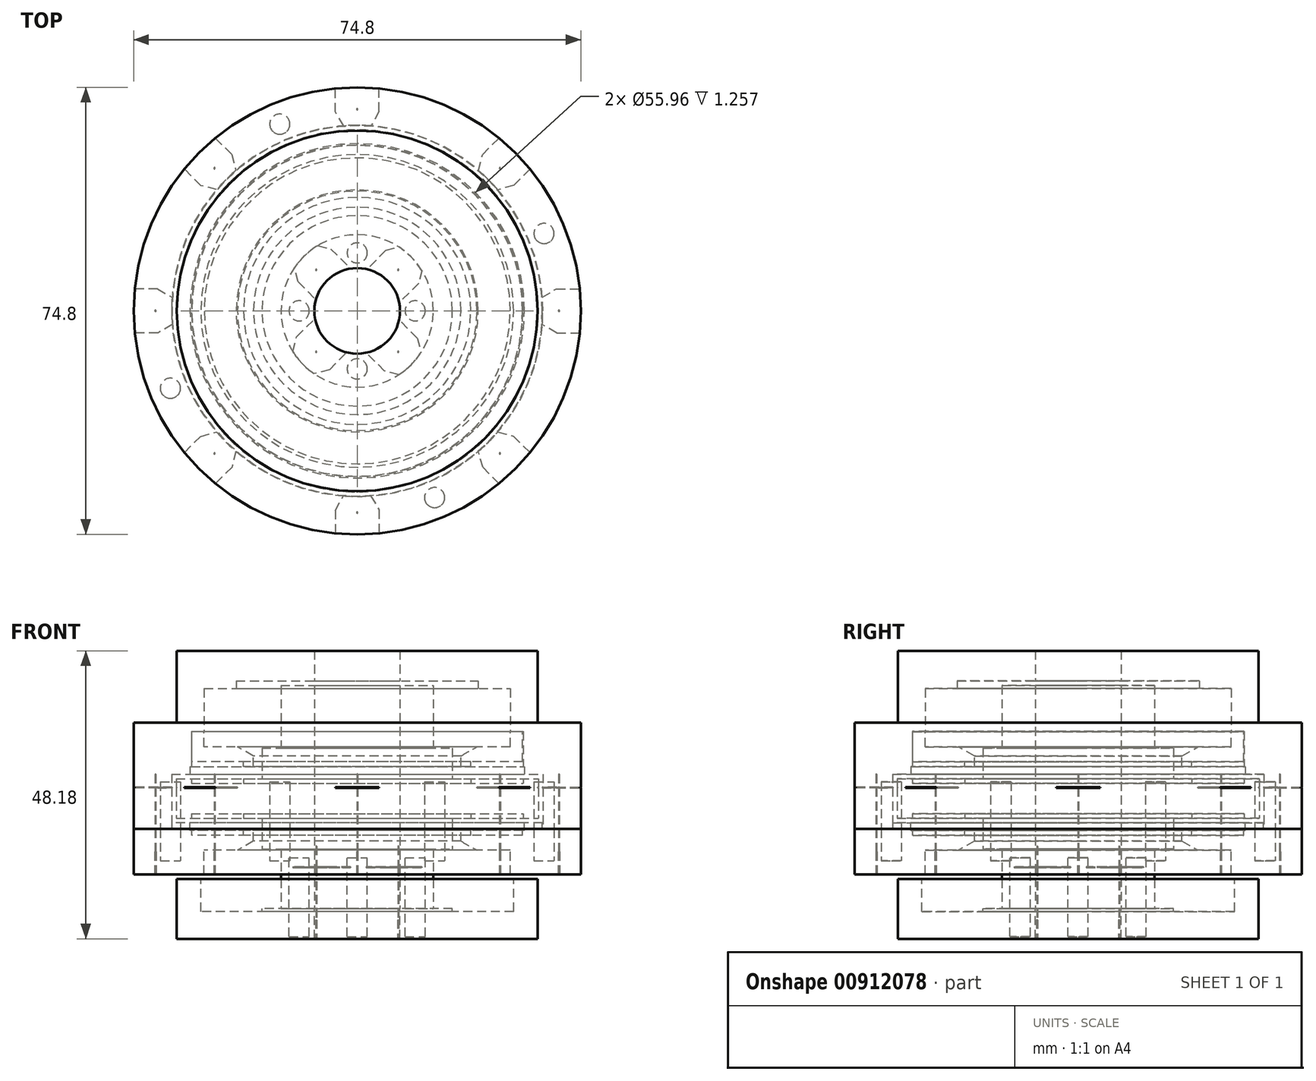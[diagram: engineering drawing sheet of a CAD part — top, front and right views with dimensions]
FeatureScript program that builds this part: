
annotation { "Feature Type Name" : "Feature", "Feature Type Description" : "" }
export const myFeature = defineFeature(function(context is Context, id is Id, definition is map)
    precondition{}
    {
        {
            assignVariable(context, id + "F0", {"name" : "CLOSE_FIT", "anyValue" : 0.01});
        }
        {
            assignVariable(context, id + "F1", {"name" : "SHRINKAGE", "anyValue" : 0});
        }
        {
            var Q0;
            Q0=qCreatedBy(makeId("Front.planeOp"),FACE);
            var sketch = newSketch(context, id + "F2", { "sketchPlane" : qUnion([Q0])});
            skLineSegment(sketch, "E0", {"start": v(-19.08, 2.54) * mm, "end": v(-19.08, 6.13) * mm});
            skLineSegment(sketch, "E1", {"start": v(-19.08, 6.13) * mm, "end": v(-27.67, 6.13) * mm});
            skLineSegment(sketch, "E2", {"start": v(-27.67, 6.13) * mm, "end": v(-27.67, 2.54) * mm});
            skLineSegment(sketch, "E3", {"start": v(-19.08, 2.54) * mm, "end": v(-27.67, 2.54) * mm});
            skLineSegment(sketch, "E4.bottom", {"start": v(-27.67, -2.54) * mm, "end": v(-19.08, -2.54) * mm});
            skLineSegment(sketch, "E4.top", {"start": v(-27.67, -6.13) * mm, "end": v(-19.08, -6.13) * mm});
            skLineSegment(sketch, "E4.left", {"start": v(-27.67, -2.54) * mm, "end": v(-27.67, -6.13) * mm});
            skLineSegment(sketch, "E4.right", {"start": v(-19.08, -2.54) * mm, "end": v(-19.08, -6.13) * mm});
            skLineSegment(sketch, "E5", {"start": v(-27.67, 5.33) * mm, "end": v(-27.93, 5.33) * mm});
            skLineSegment(sketch, "E6", {"start": v(-27.93, 5.33) * mm, "end": v(-27.93, 3.34) * mm});
            skLineSegment(sketch, "E7", {"start": v(-27.93, 3.34) * mm, "end": v(-27.67, 3.34) * mm});
            skLineSegment(sketch, "E8", {"start": v(-19.08, 5.33) * mm, "end": v(-18.83, 5.33) * mm});
            skLineSegment(sketch, "E9", {"start": v(-18.83, 5.33) * mm, "end": v(-18.83, 3.34) * mm});
            skLineSegment(sketch, "E10", {"start": v(-18.83, 3.34) * mm, "end": v(-19.08, 3.34) * mm});
            skLineSegment(sketch, "E11", {"start": v(-27.67, -3.35) * mm, "end": v(-27.93, -3.35) * mm});
            skLineSegment(sketch, "E12", {"start": v(-27.93, -3.35) * mm, "end": v(-27.93, -5.32) * mm});
            skLineSegment(sketch, "E13", {"start": v(-27.93, -5.32) * mm, "end": v(-27.67, -5.32) * mm});
            skLineSegment(sketch, "E14", {"start": v(-19.08, -3.35) * mm, "end": v(-18.83, -3.35) * mm});
            skLineSegment(sketch, "E15", {"start": v(-18.83, -3.35) * mm, "end": v(-18.83, -5.32) * mm});
            skLineSegment(sketch, "E16", {"start": v(-18.83, -5.32) * mm, "end": v(-19.08, -5.32) * mm});
            skSolve(sketch);
        }
        {
            var Q0;
            Q0=qCreatedBy(makeId("Front.planeOp"),FACE);
            var sketch = newSketch(context, id + "F3", { "sketchPlane" : qUnion([Q0])});
            skLineSegment(sketch, "E17", {"start": v(-25.4, 18.14) * mm, "end": v(-25.4, 8.67) * mm});
            skLineSegment(sketch, "E18", {"start": v(-25.4, 8.67) * mm, "end": v(-12.7, 8.67) * mm});
            skLineSegment(sketch, "E19", {"start": v(-12.7, 8.67) * mm, "end": v(-12.7, 18.14) * mm});
            skLineSegment(sketch, "E20", {"start": v(-12.7, 18.14) * mm, "end": v(-25.4, 18.14) * mm});
            skLineSegment(sketch, "E21", {"start": v(0, 0) * mm, "end": v(0, 56.46) * mm, "construction": true});
            skLineSegment(sketch, "E22.bottom", {"start": v(-25.4, -8.67) * mm, "end": v(-12.7, -8.67) * mm});
            skLineSegment(sketch, "E22.top", {"start": v(-25.4, -18.14) * mm, "end": v(-12.7, -18.14) * mm});
            skLineSegment(sketch, "E22.left", {"start": v(-25.4, -8.67) * mm, "end": v(-25.4, -18.14) * mm});
            skLineSegment(sketch, "E22.right", {"start": v(-12.7, -8.67) * mm, "end": v(-12.7, -18.14) * mm});
            skSolve(sketch);
        }
        {
            var Q0;
            Q0=qCreatedBy(makeId("Front.planeOp"),FACE);
            var sketch = newSketch(context, id + "F4", { "sketchPlane" : qUnion([Q0])});
            skLineSegment(sketch, "E23", {"start": v(-30.18, 31.75) * mm, "end": v(-26, 31.75) * mm});
            skLineSegment(sketch, "E24", {"start": v(-26, 31.75) * mm, "end": v(-26, 82.55) * mm});
            skLineSegment(sketch, "E25", {"start": v(-26, 82.55) * mm, "end": v(-30.18, 82.55) * mm});
            skLineSegment(sketch, "E26", {"start": v(-30.18, 82.55) * mm, "end": v(-30.18, 31.75) * mm});
            skLineSegment(sketch, "E27.bottom", {"start": v(-30.18, -31.75) * mm, "end": v(-26, -31.75) * mm});
            skLineSegment(sketch, "E27.top", {"start": v(-30.18, -82.55) * mm, "end": v(-26, -82.55) * mm});
            skLineSegment(sketch, "E27.left", {"start": v(-30.18, -31.75) * mm, "end": v(-30.18, -82.55) * mm});
            skLineSegment(sketch, "E27.right", {"start": v(-26, -31.75) * mm, "end": v(-26, -82.55) * mm});
            skSolve(sketch);
        }
        {
            var Q0;
            Q0=qCreatedBy(makeId("Front.planeOp"),FACE);
            var sketch = newSketch(context, id + "F5", { "sketchPlane" : qUnion([Q0])});
            skLineSegment(sketch, "E28", {"start": v(-27.75, -2.54) * mm, "end": v(-19, -2.54) * mm});
            skLineSegment(sketch, "E29", {"start": v(-12.75, -8.42) * mm, "end": v(-12.75, -18.39) * mm});
            skLineSegment(sketch, "E30", {"start": v(-27.75, 2.54) * mm, "end": v(-19, 2.54) * mm});
            skLineSegment(sketch, "E31", {"start": v(-12.75, 8.42) * mm, "end": v(-12.75, 18.9) * mm});
            skLineSegment(sketch, "E32", {"start": v(-12.75, 18.9) * mm, "end": v(-7.16, 18.9) * mm});
            skLineSegment(sketch, "E33", {"start": v(-7.16, 18.9) * mm, "end": v(-7.16, -18.39) * mm});
            skLineSegment(sketch, "E34", {"start": v(-7.16, -18.39) * mm, "end": v(-12.75, -18.39) * mm});
            skLineSegment(sketch, "E35", {"start": v(-19, 2.54) * mm, "end": v(-19, 3.33) * mm});
            skLineSegment(sketch, "E36", {"start": v(-19, 3.33) * mm, "end": v(-15.93, 3.33) * mm});
            skLineSegment(sketch, "E37", {"start": v(-15.93, 3.33) * mm, "end": v(-15.93, 8.42) * mm});
            skLineSegment(sketch, "E38", {"start": v(-15.93, 8.42) * mm, "end": v(-12.75, 8.42) * mm});
            skLineSegment(sketch, "E39", {"start": v(-19, -2.54) * mm, "end": v(-19, -3.33) * mm});
            skLineSegment(sketch, "E40", {"start": v(-19, -3.33) * mm, "end": v(-15.93, -3.33) * mm});
            skLineSegment(sketch, "E41", {"start": v(-15.93, -3.33) * mm, "end": v(-15.93, -8.42) * mm});
            skLineSegment(sketch, "E42", {"start": v(-15.93, -8.42) * mm, "end": v(-12.75, -8.42) * mm});
            skLineSegment(sketch, "E43", {"start": v(-27.75, 2.54) * mm, "end": v(-27.75, 3.33) * mm});
            skLineSegment(sketch, "E44", {"start": v(-27.75, 3.33) * mm, "end": v(-30.29, 3.33) * mm});
            skLineSegment(sketch, "E45", {"start": v(-30.29, -3.33) * mm, "end": v(-27.75, -3.33) * mm});
            skLineSegment(sketch, "E46", {"start": v(-27.75, -3.33) * mm, "end": v(-27.75, -2.54) * mm});
            skLineSegment(sketch, "E47", {"start": v(-30.29, 3.33) * mm, "end": v(-30.29, -3.33) * mm});
            skSolve(sketch);
        }
        {
            var Q0;
            Q0=qCreatedBy(makeId("Front.planeOp"),FACE);
            var sketch = newSketch(context, id + "F6", { "sketchPlane" : qUnion([Q0])});
            skLineSegment(sketch, "E48", {"start": v(-20.24, 18.39) * mm, "end": v(-25.6, 18.39) * mm});
            skLineSegment(sketch, "E49", {"start": v(-25.6, 18.39) * mm, "end": v(-25.6, 11.21) * mm});
            skLineSegment(sketch, "E50", {"start": v(-37.4, -5.08) * mm, "end": v(-31.05, -5.08) * mm});
            skLineSegment(sketch, "E51", {"start": v(-31.05, -5.08) * mm, "end": v(-31.05, 4.09) * mm});
            skLineSegment(sketch, "E52", {"start": v(-31.05, 4.09) * mm, "end": v(-27.98, 4.09) * mm});
            skLineSegment(sketch, "E53", {"start": v(-27.75, 5.35) * mm, "end": v(-27.75, 11.21) * mm});
            skLineSegment(sketch, "E54", {"start": v(-27.75, 11.21) * mm, "end": v(-25.6, 11.21) * mm});
            skLineSegment(sketch, "E55", {"start": v(-20.24, 18.39) * mm, "end": v(-20.24, 19.66) * mm});
            skLineSegment(sketch, "E56", {"start": v(-37.4, -5.08) * mm, "end": v(-37.4, 12.7) * mm});
            skLineSegment(sketch, "E57", {"start": v(-30.18, 24.71) * mm, "end": v(-30.18, 12.7) * mm});
            skLineSegment(sketch, "E58", {"start": v(-30.18, 12.7) * mm, "end": v(-37.4, 12.7) * mm});
            skLineSegment(sketch, "E59", {"start": v(0, 0) * mm, "end": v(0, 39.51) * mm, "construction": true});
            skLineSegment(sketch, "E60", {"start": v(-7.16, 24.71) * mm, "end": v(-7.16, 19.66) * mm});
            skLineSegment(sketch, "E61", {"start": v(-7.16, 19.66) * mm, "end": v(-20.24, 19.66) * mm});
            skLineSegment(sketch, "E62", {"start": v(-27.98, 4.09) * mm, "end": v(-27.98, 5.35) * mm});
            skLineSegment(sketch, "E63", {"start": v(-27.98, 5.35) * mm, "end": v(-27.75, 5.35) * mm});
            skLineSegment(sketch, "E64", {"start": v(-30.18, 24.71) * mm, "end": v(-7.16, 24.71) * mm});
            skSolve(sketch);
        }
        {
            var Q0;
            Q0=qCreatedBy(makeId("Front.planeOp"),FACE);
            var sketch = newSketch(context, id + "F7", { "sketchPlane" : qUnion([Q0])});
            skLineSegment(sketch, "E65", {"start": v(-27.67, 6.13) * mm, "end": v(-19, 6.13) * mm});
            skLineSegment(sketch, "E66", {"start": v(-17.35, 7.13) * mm, "end": v(-20.04, 8.65) * mm});
            skLineSegment(sketch, "E67", {"start": v(-20.04, 8.65) * mm, "end": v(-25.6, 8.65) * mm});
            skLineSegment(sketch, "E68", {"start": v(-25.6, 8.65) * mm, "end": v(-25.6, 11.19) * mm});
            skLineSegment(sketch, "E69", {"start": v(-25.6, 11.19) * mm, "end": v(-27.67, 11.19) * mm});
            skLineSegment(sketch, "E70", {"start": v(-27.67, 11.19) * mm, "end": v(-27.67, 6.13) * mm});
            skLineSegment(sketch, "E71", {"start": v(-19, 6.13) * mm, "end": v(-19, 5.35) * mm});
            skLineSegment(sketch, "E72", {"start": v(-19, 5.35) * mm, "end": v(-17.35, 5.35) * mm});
            skLineSegment(sketch, "E73", {"start": v(-17.35, 5.35) * mm, "end": v(-17.35, 7.13) * mm});
            skLineSegment(sketch, "E74", {"start": v(-30.05, 0) * mm, "end": v(0, 0) * mm, "construction": true});
            skLineSegment(sketch, "E75.MirrorCS", {"start": v(-19, -5.35) * mm, "end": v(-17.35, -5.35) * mm, "construction": true});
            skLineSegment(sketch, "E76.MirrorCS", {"start": v(-19, -6.13) * mm, "end": v(-19, -5.35) * mm, "construction": true});
            skLineSegment(sketch, "E77.MirrorCS", {"start": v(-25.6, -8.65) * mm, "end": v(-25.6, -11.19) * mm, "construction": true});
            skLineSegment(sketch, "E78.MirrorCS", {"start": v(-25.6, -11.19) * mm, "end": v(-27.67, -11.19) * mm, "construction": true});
            skLineSegment(sketch, "E79.MirrorCS", {"start": v(-17.35, -5.35) * mm, "end": v(-17.35, -7.13) * mm, "construction": true});
            skLineSegment(sketch, "E80.MirrorCS", {"start": v(-27.67, -6.13) * mm, "end": v(-19, -6.13) * mm, "construction": true});
            skLineSegment(sketch, "E81.MirrorCS", {"start": v(-20.04, -8.65) * mm, "end": v(-25.6, -8.65) * mm, "construction": true});
            skLineSegment(sketch, "E82.MirrorCS", {"start": v(-27.67, -11.19) * mm, "end": v(-27.67, -6.13) * mm, "construction": true});
            skLineSegment(sketch, "E83.MirrorCS", {"start": v(-17.35, -7.13) * mm, "end": v(-20.04, -8.65) * mm, "construction": true});
            skLineSegment(sketch, "E84", {"start": v(0, 19.57) * mm, "end": v(0, -21.08) * mm, "construction": true});
            skSolve(sketch);
        }
        {
            var Q0;
            Q0=qCreatedBy(makeId("Front.planeOp"),FACE);
            var sketch = newSketch(context, id + "F8", { "sketchPlane" : qUnion([Q0])});
            skLineSegment(sketch, "E85", {"start": v(-27.67, -11.19) * mm, "end": v(-25.6, -11.19) * mm});
            skLineSegment(sketch, "E86", {"start": v(-25.6, -11.19) * mm, "end": v(-25.6, -12.7) * mm});
            skLineSegment(sketch, "E87", {"start": v(-37.4, -5.1) * mm, "end": v(-37.4, -12.7) * mm});
            skLineSegment(sketch, "E88", {"start": v(-37.4, -12.7) * mm, "end": v(-25.6, -12.7) * mm});
            skLineSegment(sketch, "E89", {"start": v(-37.4, -5.1) * mm, "end": v(-30.98, -5.1) * mm});
            skLineSegment(sketch, "E90", {"start": v(-30.98, -4.09) * mm, "end": v(-27.98, -4.09) * mm});
            skLineSegment(sketch, "E91", {"start": v(-27.67, -5.35) * mm, "end": v(-27.67, -11.19) * mm});
            skLineSegment(sketch, "E92", {"start": v(0, 0) * mm, "end": v(0, -37.72) * mm, "construction": true});
            skLineSegment(sketch, "E93", {"start": v(-27.98, -4.09) * mm, "end": v(-27.98, -5.35) * mm});
            skLineSegment(sketch, "E94", {"start": v(-27.98, -5.35) * mm, "end": v(-27.67, -5.35) * mm});
            skLineSegment(sketch, "E95", {"start": v(-30.98, -4.09) * mm, "end": v(-30.98, -5.1) * mm});
            skLineSegment(sketch, "E96", {"start": v(-25.6, -11.19) * mm, "end": v(-25.6, -8.65) * mm});
            skLineSegment(sketch, "E97", {"start": v(-25.6, -8.65) * mm, "end": v(-20.04, -8.65) * mm});
            skLineSegment(sketch, "E98", {"start": v(-20.04, -8.65) * mm, "end": v(-17.35, -7.13) * mm});
            skLineSegment(sketch, "E99", {"start": v(-17.35, -7.13) * mm, "end": v(-17.35, -5.35) * mm});
            skLineSegment(sketch, "E100", {"start": v(-17.35, -5.35) * mm, "end": v(-19, -5.35) * mm});
            skLineSegment(sketch, "E101", {"start": v(-19, -5.35) * mm, "end": v(-19, -6.13) * mm});
            skLineSegment(sketch, "E102", {"start": v(-19, -6.13) * mm, "end": v(-27.67, -6.13) * mm});
            skSolve(sketch);
        }
        {
            var Q0;
            Q0=qCreatedBy(makeId("Front.planeOp"),FACE);
            var sketch = newSketch(context, id + "F9", { "sketchPlane" : qUnion([Q0])});
            skLineSegment(sketch, "E103", {"start": v(-7.16, -23.47) * mm, "end": v(-7.16, -18.41) * mm});
            skLineSegment(sketch, "E104", {"start": v(-7.16, -23.47) * mm, "end": v(-30.18, -23.47) * mm});
            skLineSegment(sketch, "E105", {"start": v(-30.18, -23.47) * mm, "end": v(-30.18, -13.46) * mm});
            skLineSegment(sketch, "E106", {"start": v(-15.93, -18.41) * mm, "end": v(-7.16, -18.41) * mm});
            skLineSegment(sketch, "E107", {"start": v(0, 0) * mm, "end": v(0, -37.8) * mm, "construction": true});
            skLineSegment(sketch, "E108", {"start": v(-15.93, -18.41) * mm, "end": v(-15.93, -18.9) * mm});
            skLineSegment(sketch, "E109", {"start": v(-30.18, -13.46) * mm, "end": v(-26.16, -13.46) * mm});
            skLineSegment(sketch, "E110", {"start": v(-26.16, -13.46) * mm, "end": v(-26.16, -18.9) * mm});
            skLineSegment(sketch, "E111", {"start": v(-26.16, -18.9) * mm, "end": v(-15.93, -18.9) * mm});
            skSolve(sketch);
        }
        {
            var Q0;
            Q0=makeQuery(id+"F5.imprint","IMPRINT",FACE,{"disambiguationData":[TD([[makeQuery(id+"F5.imprint","IMPRINT",EDGE,{"derivedFrom":sQuery(id+"F5.wireOp",EDGE,"E28")}),1.0]])]});
            var Q1;
            Q1=sQuery(id+"F3.wireOp",EDGE,"E21");
            revolve(context, id + "F10", {"surfaceOperationType" : NewSurfaceOperationType.NEW, "entities" : qUnion([Q0]), "axis" : qUnion([Q1]), "revolveType" : RevolveType.FULL});
        }
        {
            var Q0;
            Q0=makeQuery(id+"F9.imprint","IMPRINT",FACE,{"disambiguationData":[TD([[makeQuery(id+"F9.imprint","IMPRINT",EDGE,{"derivedFrom":sQuery(id+"F9.wireOp",EDGE,"E103")}),1.0]])]});
            var Q1;
            Q1=sQuery(id+"F8.wireOp",EDGE,"E92");
            revolve(context, id + "F11", {"operationType" : NewBodyOperationType.ADD, "surfaceOperationType" : NewSurfaceOperationType.NEW, "entities" : qUnion([Q0]), "axis" : qUnion([Q1]), "revolveType" : RevolveType.FULL});
        }
        {
            var Q0;
            Q0=makeQuery(id+"F10.opRevolve","SWEPT_FACE",FACE,{"disambiguationData":[OSD([sQuery(id+"F5.wireOp",EDGE,"E34")])]});
            var sketch = newSketch(context, id + "F12", { "sketchPlane" : qUnion([Q0])});
            skCircle(sketch, "E112", {"center": v(0, 9.7) * mm, "radius": 1.69 * mm});
            skCircle(sketch, "E113.1.0", {"center": v(9.7, 0) * mm, "radius": 1.69 * mm});
            skCircle(sketch, "E113.2.0", {"center": v(0, -9.7) * mm, "radius": 1.69 * mm});
            skCircle(sketch, "E113.3.0", {"center": v(-9.7, 0) * mm, "radius": 1.69 * mm});
            skPoint(sketch, "E113.center", {"position": v(0, 0) * mm});
            skLineSegment(sketch, "E113.anchor1", {"start": v(0, 0) * mm, "end": v(0, 9.7) * mm, "construction": true});
            skLineSegment(sketch, "E113.anchor2", {"start": v(0, 0) * mm, "end": v(-9.7, 0) * mm, "construction": true});
            skCircle(sketch, "E114", {"center": v(0, 0) * mm, "radius": 9.7 * mm, "construction": true});
            skSolve(sketch);
        }
        {
            var Q0;
            Q0 = qSketchRegion(id + "F12", true);
            extrude(context, id + "F13", {"entities" : qUnion([Q0]), "operationType" : NewBodyOperationType.REMOVE, "depth" : 4.7 * mm, "offsetDistance" : 25.4 * mm, "hasSecondDirection" : true, "secondDirectionOppositeDirection" : true, "secondDirectionDepth" : 8.5 * mm});
        }
        {
            var Q0;
            Q0=makeQuery(id+"F11.opRevolve","SWEPT_FACE",FACE,{"disambiguationData":[OSD([sQuery(id+"F9.wireOp",EDGE,"E104")])]});
            var sketch = newSketch(context, id + "F14", { "sketchPlane" : qUnion([Q0])});
            skCircle(sketch, "E115", {"center": v(0, 0) * mm, "radius": 9.7 * mm, "construction": true});
            skLineSegment(sketch, "E116", {"start": v(0, 0) * mm, "end": v(6.86, 6.86) * mm, "construction": true});
            skLineSegment(sketch, "E117", {"start": v(0, 0) * mm, "end": v(0, 9.7) * mm, "construction": true});
            skPoint(sketch, "E118", {"position": v(6.86, 6.86) * mm});
            skPoint(sketch, "E119.1.0", {"position": v(-6.86, 6.86) * mm});
            skPoint(sketch, "E119.2.0", {"position": v(-6.86, -6.86) * mm});
            skPoint(sketch, "E119.3.0", {"position": v(6.86, -6.86) * mm});
            skSolve(sketch);
        }
        {
            var Q0;
            Q0=sQuery(id+"F14.wireOp",VERTEX,"E119.1.0");
            var Q1;
            Q1=sQuery(id+"F14.wireOp",VERTEX,"E119.2.0");
            var Q2;
            Q2=sQuery(id+"F14.wireOp",VERTEX,"E119.3.0");
            var Q3;
            Q3=sQuery(id+"F14.wireOp",VERTEX,"E118");
            var Q4;
            Q4=makeQuery(id+"F10.opRevolve","SWEPT_BODY",BODY,{"disambiguationData":[OSD([sQuery(id+"F5.wireOp",EDGE,"E28"),sQuery(id+"F5.wireOp",EDGE,"E29"),sQuery(id+"F5.wireOp",EDGE,"E30"),sQuery(id+"F5.wireOp",EDGE,"E31"),sQuery(id+"F5.wireOp",EDGE,"E32"),sQuery(id+"F5.wireOp",EDGE,"E33"),sQuery(id+"F5.wireOp",EDGE,"E34"),sQuery(id+"F5.wireOp",EDGE,"E35"),sQuery(id+"F5.wireOp",EDGE,"E36"),sQuery(id+"F5.wireOp",EDGE,"E37"),sQuery(id+"F5.wireOp",EDGE,"E38"),sQuery(id+"F5.wireOp",EDGE,"E39"),sQuery(id+"F5.wireOp",EDGE,"E40"),sQuery(id+"F5.wireOp",EDGE,"E41"),sQuery(id+"F5.wireOp",EDGE,"E42"),sQuery(id+"F5.wireOp",EDGE,"E43"),sQuery(id+"F5.wireOp",EDGE,"E44"),sQuery(id+"F5.wireOp",EDGE,"E45"),sQuery(id+"F5.wireOp",EDGE,"E46"),sQuery(id+"F5.wireOp",EDGE,"E47")])]});
            var Q5;
            Q5=makeQuery(id+"F11.opRevolve","SWEPT_BODY",BODY,{"disambiguationData":[OSD([sQuery(id+"F9.wireOp",EDGE,"E103"),sQuery(id+"F9.wireOp",EDGE,"6eMewhFd-rIyQ-tEOm-2qX8-bQ4E5q1Qq0mu"),sQuery(id+"F9.wireOp",EDGE,"E104"),sQuery(id+"F9.wireOp",EDGE,"E105"),sQuery(id+"F9.wireOp",EDGE,"nJ21CKZv-7VvW-SMsm-240K-6D86ggK8eWdG"),sQuery(id+"F9.wireOp",EDGE,"E106")])]});
            hole(context, id + "F15", {"style" : HoleStyle.C_BORE, "endStyle" : HoleEndStyle.BLIND, "holeDiameter" : (.118 + getVariable(context, 'SHRINKAGE') + getVariable(context, 'CLOSE_FIT')) * mm, "cBoreDiameter" : (.18 + getVariable(context, 'SHRINKAGE') + getVariable(context, 'CLOSE_FIT')) * mm, "cBoreDepth" : 3.17 * mm, "majorDiameter" : 6.35 * mm, "holeDepth" : 15.5 * mm, "isTappedThrough" : true, "tappedDepth" : 12.7 * mm, "tapClearance" : 3, "locations" : qUnion([Q0, Q1, Q2, Q3]), "scope" : qUnion([Q4, Q5])});
        }
        {
            var Q0;
            Q0=makeQuery(id+"F6.imprint","IMPRINT",FACE,{"disambiguationData":[TD([[makeQuery(id+"F6.imprint","IMPRINT",EDGE,{"derivedFrom":sQuery(id+"F6.wireOp",EDGE,"E48")}),-1.0]])]});
            var Q1;
            Q1=sQuery(id+"F6.wireOp",EDGE,"E59");
            revolve(context, id + "F16", {"surfaceOperationType" : NewSurfaceOperationType.NEW, "entities" : qUnion([Q0]), "axis" : qUnion([Q1]), "revolveType" : RevolveType.FULL});
        }
        {
            var Q0;
            Q0=makeQuery(id+"F8.imprint","IMPRINT",FACE,{"disambiguationData":[TD([[makeQuery(id+"F8.imprint","IMPRINT",EDGE,{"derivedFrom":sQuery(id+"F8.wireOp",EDGE,"E85")}),-1.0]])]});
            var Q1;
            {var subQ0=sQuery(id+"F8.wireOp",EDGE,"E85");Q1=makeQuery(id+"F8.imprint","IMPRINT",FACE,{"disambiguationData":[TD([[makeQuery(id+"F8.imprint","IMPRINT",EDGE,{"derivedFrom":subQ0}),1.0]])]});}
            var Q2;
            Q2=sQuery(id+"F8.wireOp",EDGE,"E92");
            revolve(context, id + "F17", {"operationType" : NewBodyOperationType.ADD, "surfaceOperationType" : NewSurfaceOperationType.NEW, "entities" : qUnion([Q0, Q1]), "axis" : qUnion([Q2]), "revolveType" : RevolveType.FULL});
        }
        {
            var Q0;
            Q0 = qSketchRegion(id + "F7", true);
            var Q1;
            Q1=sQuery(id+"F7.wireOp",EDGE,"E84");
            revolve(context, id + "F18", {"surfaceOperationType" : NewSurfaceOperationType.NEW, "entities" : qUnion([Q0]), "axis" : qUnion([Q1]), "revolveType" : RevolveType.FULL});
        }
        {
            var Q0;
            Q0=makeQuery(id+"F17.opRevolve","SWEPT_FACE",FACE,{"disambiguationData":[OSD([sQuery(id+"F8.wireOp",EDGE,"E88")])]});
            var sketch = newSketch(context, id + "F19", { "sketchPlane" : qUnion([Q0])});
            skCircle(sketch, "E120", {"center": v(0, 0) * mm, "radius": 33.75 * mm, "construction": true});
            skPoint(sketch, "E121", {"position": v(0, 33.75) * mm});
            skPoint(sketch, "E122.1.0", {"position": v(-23.87, 23.87) * mm});
            skPoint(sketch, "E122.2.0", {"position": v(-33.75, 0) * mm});
            skPoint(sketch, "E122.3.0", {"position": v(-23.87, -23.87) * mm});
            skPoint(sketch, "E122.4.0", {"position": v(0, -33.75) * mm});
            skPoint(sketch, "E122.5.0", {"position": v(23.87, -23.87) * mm});
            skPoint(sketch, "E122.6.0", {"position": v(33.75, 0) * mm});
            skPoint(sketch, "E122.7.0", {"position": v(23.87, 23.87) * mm});
            skSolve(sketch);
        }
        {
            var Q0;
            Q0=sQuery(id+"F19.wireOp",VERTEX,"E121");
            var Q1;
            Q1=sQuery(id+"F19.wireOp",VERTEX,"E122.1.0");
            var Q2;
            Q2=sQuery(id+"F19.wireOp",VERTEX,"E122.2.0");
            var Q3;
            Q3=sQuery(id+"F19.wireOp",VERTEX,"E122.3.0");
            var Q4;
            Q4=sQuery(id+"F19.wireOp",VERTEX,"E122.4.0");
            var Q5;
            Q5=sQuery(id+"F19.wireOp",VERTEX,"E122.5.0");
            var Q6;
            Q6=sQuery(id+"F19.wireOp",VERTEX,"E122.6.0");
            var Q7;
            Q7=sQuery(id+"F19.wireOp",VERTEX,"E122.7.0");
            var Q8;
            Q8=makeQuery(id+"F16.opRevolve","SWEPT_BODY",BODY,{"disambiguationData":[OSD([sQuery(id+"F6.wireOp",EDGE,"E48"),sQuery(id+"F6.wireOp",EDGE,"E49"),sQuery(id+"F6.wireOp",EDGE,"E50"),sQuery(id+"F6.wireOp",EDGE,"E51"),sQuery(id+"F6.wireOp",EDGE,"E52"),sQuery(id+"F6.wireOp",EDGE,"E53"),sQuery(id+"F6.wireOp",EDGE,"E54"),sQuery(id+"F6.wireOp",EDGE,"E55"),sQuery(id+"F6.wireOp",EDGE,"E56"),sQuery(id+"F6.wireOp",EDGE,"ZNaOq2wC-KwrG-OMNd-pMAv-wtNMxdYC1MxH"),sQuery(id+"F6.wireOp",EDGE,"E57"),sQuery(id+"F6.wireOp",EDGE,"E58"),sQuery(id+"F6.wireOp",EDGE,"evgzWDB2-6hjm-w7Me-QYDy-q4x9oqQhbVmM"),sQuery(id+"F6.wireOp",EDGE,"E60"),sQuery(id+"F6.wireOp",EDGE,"E61")])]});
            var Q9;
            Q9=makeQuery(id+"F17.opRevolve","SWEPT_BODY",BODY,{"disambiguationData":[OSD([sQuery(id+"F8.wireOp",EDGE,"E85"),sQuery(id+"F8.wireOp",EDGE,"E86"),sQuery(id+"F8.wireOp",EDGE,"CwQqnWJK-n9GY-hT4R-4o8w-eWMCeK6YaEPR"),sQuery(id+"F8.wireOp",EDGE,"UTAAZTBJ-55EI-9GvV-iKB0-o1MeyqjgZGp4"),sQuery(id+"F8.wireOp",EDGE,"E87"),sQuery(id+"F8.wireOp",EDGE,"E88"),sQuery(id+"F8.wireOp",EDGE,"ciWuzBY4-idQ8-rcUr-xRdj-Jt2UZL75m4BT"),sQuery(id+"F8.wireOp",EDGE,"JA3ulJ37-WCai-hBDu-FBNc-0sG8ukCFW5zY"),sQuery(id+"F8.wireOp",EDGE,"E89"),sQuery(id+"F8.wireOp",EDGE,"5QXMWiV2-a3HE-DiGb-4yEv-sN6Ab6hOUnc0"),sQuery(id+"F8.wireOp",EDGE,"E90"),sQuery(id+"F8.wireOp",EDGE,"E91")])]});
            hole(context, id + "F20", {"style" : HoleStyle.C_BORE, "endStyle" : HoleEndStyle.BLIND, "holeDiameter" : (.118 + getVariable(context, 'SHRINKAGE') + getVariable(context, 'CLOSE_FIT')) * mm, "cBoreDiameter" : (.195 + getVariable(context, 'SHRINKAGE') + getVariable(context, 'CLOSE_FIT')) * mm, "cBoreDepth" : 3.8 * mm, "majorDiameter" : 6.35 * mm, "holeDepth" : 16.76 * mm, "isTappedThrough" : true, "tappedDepth" : 12.7 * mm, "tapClearance" : 3, "locations" : qUnion([Q0, Q1, Q2, Q3, Q4, Q5, Q6, Q7]), "scope" : qUnion([Q8, Q9])});
        }
        {
            var Q0;
            Q0=makeQuery(id+"F16.opRevolve","SWEPT_FACE",FACE,{"disambiguationData":[OSD([sQuery(id+"F6.wireOp",EDGE,"E50")])]});
            var sketch = newSketch(context, id + "F21", { "sketchPlane" : qUnion([Q0])});
            skLineSegment(sketch, "E123", {"start": v(0, 0) * mm, "end": v(0, 38.83) * mm, "construction": true});
            skLineSegment(sketch, "E124", {"start": v(0, 0) * mm, "end": v(15.35, 37.07) * mm, "construction": true});
            skCircle(sketch, "E125", {"center": v(0, 0) * mm, "radius": 33.83 * mm, "construction": true});
            skCircle(sketch, "E126", {"center": v(12.94, 31.25) * mm, "radius": 1.69 * mm});
            skCircle(sketch, "E127.1.0", {"center": v(-31.25, 12.94) * mm, "radius": 1.69 * mm});
            skCircle(sketch, "E127.2.0", {"center": v(-12.94, -31.25) * mm, "radius": 1.69 * mm});
            skCircle(sketch, "E127.3.0", {"center": v(31.25, -12.94) * mm, "radius": 1.69 * mm});
            skSolve(sketch);
        }
        {
            var Q0;
            Q0 = qSketchRegion(id + "F21", true);
            extrude(context, id + "F22", {"entities" : qUnion([Q0]), "operationType" : NewBodyOperationType.REMOVE, "oppositeDirection" : true, "depth" : 7.87 * mm, "offsetDistance" : 25.4 * mm, "hasSecondDirection" : true, "secondDirectionOppositeDirection" : false, "secondDirectionDepth" : 5.33 * mm});
        }
        {
            var Q0;
            Q0=qCreatedBy(makeId("Top.planeOp"),FACE);
            cPlane(context, id + "F23", {"entities" : qUnion([Q0]), "cplaneType" : CPlaneType.OFFSET, "offset" : 1.9 * mm, "width" : 152.4 * mm, "height" : 152.4 * mm});
        }
        {
            var Q0;
            Q0=qCreatedBy(id+"F23.planeOp",FACE);
            var sketch = newSketch(context, id + "F24", { "sketchPlane" : qUnion([Q0])});
            skCircle(sketch, "E128.cCircle", {"center": v(0, -33.35) * mm, "radius": 3.18 * mm, "construction": true});
            skLineSegment(sketch, "E128.0", {"start": v(-1.8, -36.54) * mm, "end": v(-3.67, -33.39) * mm, "construction": true});
            skLineSegment(sketch, "E128.1", {"start": v(-3.67, -33.39) * mm, "end": v(-1.87, -30.2) * mm});
            skLineSegment(sketch, "E128.2", {"start": v(-1.87, -30.2) * mm, "end": v(1.8, -30.16) * mm});
            skLineSegment(sketch, "E128.3", {"start": v(1.8, -30.16) * mm, "end": v(3.67, -33.31) * mm});
            skLineSegment(sketch, "E128.4", {"start": v(3.67, -33.31) * mm, "end": v(1.87, -36.5) * mm, "construction": true});
            skLineSegment(sketch, "E128.5", {"start": v(1.87, -36.5) * mm, "end": v(-1.8, -36.54) * mm, "construction": true});
            skPoint(sketch, "E128.0.midPoint", {"position": v(-2.73, -34.97) * mm});
            skLineSegment(sketch, "E129", {"start": v(-3.67, -33.39) * mm, "end": v(-3.67, -39.85) * mm});
            skLineSegment(sketch, "E130", {"start": v(3.67, -33.31) * mm, "end": v(3.67, -39.85) * mm});
            skLineSegment(sketch, "E131", {"start": v(3.67, -39.85) * mm, "end": v(-3.67, -39.85) * mm});
            skLineSegment(sketch, "E132.1.0", {"start": v(26.15, -20.96) * mm, "end": v(27.13, -24.5) * mm, "construction": true});
            skCircle(sketch, "E132.1.1", {"center": v(23.58, -23.58) * mm, "radius": 3.18 * mm, "construction": true});
            skLineSegment(sketch, "E132.1.2", {"start": v(27.13, -24.5) * mm, "end": v(24.57, -27.11) * mm, "construction": true});
            skPoint(sketch, "E132.1.3", {"position": v(22.8, -26.66) * mm});
            skLineSegment(sketch, "E132.1.4", {"start": v(30.77, -25.59) * mm, "end": v(25.59, -30.77) * mm});
            skLineSegment(sketch, "E132.1.5", {"start": v(26.15, -20.96) * mm, "end": v(30.77, -25.59) * mm});
            skLineSegment(sketch, "E132.1.6", {"start": v(21.02, -26.2) * mm, "end": v(25.59, -30.77) * mm});
            skLineSegment(sketch, "E132.1.7", {"start": v(22.6, -20.05) * mm, "end": v(26.15, -20.96) * mm});
            skLineSegment(sketch, "E132.1.8", {"start": v(21.02, -26.2) * mm, "end": v(20.03, -22.67) * mm});
            skLineSegment(sketch, "E132.1.9", {"start": v(20.03, -22.67) * mm, "end": v(22.6, -20.05) * mm});
            skLineSegment(sketch, "E132.1.10", {"start": v(24.57, -27.11) * mm, "end": v(21.02, -26.2) * mm, "construction": true});
            skLineSegment(sketch, "E132.2.0", {"start": v(33.31, 3.67) * mm, "end": v(36.5, 1.87) * mm, "construction": true});
            skCircle(sketch, "E132.2.1", {"center": v(33.35, 0) * mm, "radius": 3.18 * mm, "construction": true});
            skLineSegment(sketch, "E132.2.2", {"start": v(36.5, 1.87) * mm, "end": v(36.54, -1.8) * mm, "construction": true});
            skPoint(sketch, "E132.2.3", {"position": v(34.97, -2.73) * mm});
            skLineSegment(sketch, "E132.2.4", {"start": v(39.85, 3.67) * mm, "end": v(39.85, -3.67) * mm});
            skLineSegment(sketch, "E132.2.5", {"start": v(33.31, 3.67) * mm, "end": v(39.85, 3.67) * mm});
            skLineSegment(sketch, "E132.2.6", {"start": v(33.39, -3.67) * mm, "end": v(39.85, -3.67) * mm});
            skLineSegment(sketch, "E132.2.7", {"start": v(30.16, 1.8) * mm, "end": v(33.31, 3.67) * mm});
            skLineSegment(sketch, "E132.2.8", {"start": v(33.39, -3.67) * mm, "end": v(30.2, -1.87) * mm});
            skLineSegment(sketch, "E132.2.9", {"start": v(30.2, -1.87) * mm, "end": v(30.16, 1.8) * mm});
            skLineSegment(sketch, "E132.2.10", {"start": v(36.54, -1.8) * mm, "end": v(33.39, -3.67) * mm, "construction": true});
            skLineSegment(sketch, "E132.3.0", {"start": v(20.96, 26.15) * mm, "end": v(24.5, 27.13) * mm, "construction": true});
            skCircle(sketch, "E132.3.1", {"center": v(23.58, 23.58) * mm, "radius": 3.18 * mm, "construction": true});
            skLineSegment(sketch, "E132.3.2", {"start": v(24.5, 27.13) * mm, "end": v(27.11, 24.57) * mm, "construction": true});
            skPoint(sketch, "E132.3.3", {"position": v(26.66, 22.8) * mm});
            skLineSegment(sketch, "E132.3.4", {"start": v(25.59, 30.77) * mm, "end": v(30.77, 25.59) * mm});
            skLineSegment(sketch, "E132.3.5", {"start": v(20.96, 26.15) * mm, "end": v(25.59, 30.77) * mm});
            skLineSegment(sketch, "E132.3.6", {"start": v(26.2, 21.02) * mm, "end": v(30.77, 25.59) * mm});
            skLineSegment(sketch, "E132.3.7", {"start": v(20.05, 22.6) * mm, "end": v(20.96, 26.15) * mm});
            skLineSegment(sketch, "E132.3.8", {"start": v(26.2, 21.02) * mm, "end": v(22.67, 20.03) * mm});
            skLineSegment(sketch, "E132.3.9", {"start": v(22.67, 20.03) * mm, "end": v(20.05, 22.6) * mm});
            skLineSegment(sketch, "E132.3.10", {"start": v(27.11, 24.57) * mm, "end": v(26.2, 21.02) * mm, "construction": true});
            skLineSegment(sketch, "E132.4.0", {"start": v(-3.67, 33.31) * mm, "end": v(-1.87, 36.5) * mm, "construction": true});
            skCircle(sketch, "E132.4.1", {"center": v(0, 33.35) * mm, "radius": 3.18 * mm, "construction": true});
            skLineSegment(sketch, "E132.4.2", {"start": v(-1.87, 36.5) * mm, "end": v(1.8, 36.54) * mm, "construction": true});
            skPoint(sketch, "E132.4.3", {"position": v(2.73, 34.97) * mm});
            skLineSegment(sketch, "E132.4.4", {"start": v(-3.67, 39.85) * mm, "end": v(3.67, 39.85) * mm});
            skLineSegment(sketch, "E132.4.5", {"start": v(-3.67, 33.31) * mm, "end": v(-3.67, 39.85) * mm});
            skLineSegment(sketch, "E132.4.6", {"start": v(3.67, 33.39) * mm, "end": v(3.67, 39.85) * mm});
            skLineSegment(sketch, "E132.4.7", {"start": v(-1.8, 30.16) * mm, "end": v(-3.67, 33.31) * mm});
            skLineSegment(sketch, "E132.4.8", {"start": v(3.67, 33.39) * mm, "end": v(1.87, 30.2) * mm});
            skLineSegment(sketch, "E132.4.9", {"start": v(1.87, 30.2) * mm, "end": v(-1.8, 30.16) * mm});
            skLineSegment(sketch, "E132.4.10", {"start": v(1.8, 36.54) * mm, "end": v(3.67, 33.39) * mm, "construction": true});
            skLineSegment(sketch, "E132.5.0", {"start": v(-26.15, 20.96) * mm, "end": v(-27.13, 24.5) * mm, "construction": true});
            skCircle(sketch, "E132.5.1", {"center": v(-23.58, 23.58) * mm, "radius": 3.18 * mm, "construction": true});
            skLineSegment(sketch, "E132.5.2", {"start": v(-27.13, 24.5) * mm, "end": v(-24.57, 27.11) * mm, "construction": true});
            skPoint(sketch, "E132.5.3", {"position": v(-22.8, 26.66) * mm});
            skLineSegment(sketch, "E132.5.4", {"start": v(-30.77, 25.59) * mm, "end": v(-25.59, 30.77) * mm});
            skLineSegment(sketch, "E132.5.5", {"start": v(-26.15, 20.96) * mm, "end": v(-30.77, 25.59) * mm});
            skLineSegment(sketch, "E132.5.6", {"start": v(-21.02, 26.2) * mm, "end": v(-25.59, 30.77) * mm});
            skLineSegment(sketch, "E132.5.7", {"start": v(-22.6, 20.05) * mm, "end": v(-26.15, 20.96) * mm});
            skLineSegment(sketch, "E132.5.8", {"start": v(-21.02, 26.2) * mm, "end": v(-20.03, 22.67) * mm});
            skLineSegment(sketch, "E132.5.9", {"start": v(-20.03, 22.67) * mm, "end": v(-22.6, 20.05) * mm});
            skLineSegment(sketch, "E132.5.10", {"start": v(-24.57, 27.11) * mm, "end": v(-21.02, 26.2) * mm, "construction": true});
            skLineSegment(sketch, "E132.6.0", {"start": v(-33.31, -3.67) * mm, "end": v(-36.5, -1.87) * mm, "construction": true});
            skCircle(sketch, "E132.6.1", {"center": v(-33.35, 0) * mm, "radius": 3.18 * mm, "construction": true});
            skLineSegment(sketch, "E132.6.2", {"start": v(-36.5, -1.87) * mm, "end": v(-36.54, 1.8) * mm, "construction": true});
            skPoint(sketch, "E132.6.3", {"position": v(-34.97, 2.73) * mm});
            skLineSegment(sketch, "E132.6.4", {"start": v(-39.85, -3.67) * mm, "end": v(-39.85, 3.67) * mm});
            skLineSegment(sketch, "E132.6.5", {"start": v(-33.31, -3.67) * mm, "end": v(-39.85, -3.67) * mm});
            skLineSegment(sketch, "E132.6.6", {"start": v(-33.39, 3.67) * mm, "end": v(-39.85, 3.67) * mm});
            skLineSegment(sketch, "E132.6.7", {"start": v(-30.16, -1.8) * mm, "end": v(-33.31, -3.67) * mm});
            skLineSegment(sketch, "E132.6.8", {"start": v(-33.39, 3.67) * mm, "end": v(-30.2, 1.87) * mm});
            skLineSegment(sketch, "E132.6.9", {"start": v(-30.2, 1.87) * mm, "end": v(-30.16, -1.8) * mm});
            skLineSegment(sketch, "E132.6.10", {"start": v(-36.54, 1.8) * mm, "end": v(-33.39, 3.67) * mm, "construction": true});
            skLineSegment(sketch, "E132.7.0", {"start": v(-20.96, -26.15) * mm, "end": v(-24.5, -27.13) * mm, "construction": true});
            skCircle(sketch, "E132.7.1", {"center": v(-23.58, -23.58) * mm, "radius": 3.18 * mm, "construction": true});
            skLineSegment(sketch, "E132.7.2", {"start": v(-24.5, -27.13) * mm, "end": v(-27.11, -24.57) * mm, "construction": true});
            skPoint(sketch, "E132.7.3", {"position": v(-26.66, -22.8) * mm});
            skLineSegment(sketch, "E132.7.4", {"start": v(-25.59, -30.77) * mm, "end": v(-30.77, -25.59) * mm});
            skLineSegment(sketch, "E132.7.5", {"start": v(-20.96, -26.15) * mm, "end": v(-25.59, -30.77) * mm});
            skLineSegment(sketch, "E132.7.6", {"start": v(-26.2, -21.02) * mm, "end": v(-30.77, -25.59) * mm});
            skLineSegment(sketch, "E132.7.7", {"start": v(-20.05, -22.6) * mm, "end": v(-20.96, -26.15) * mm});
            skLineSegment(sketch, "E132.7.8", {"start": v(-26.2, -21.02) * mm, "end": v(-22.67, -20.03) * mm});
            skLineSegment(sketch, "E132.7.9", {"start": v(-22.67, -20.03) * mm, "end": v(-20.05, -22.6) * mm});
            skLineSegment(sketch, "E132.7.10", {"start": v(-27.11, -24.57) * mm, "end": v(-26.2, -21.02) * mm, "construction": true});
            skPoint(sketch, "E132.center", {"position": v(0, 0) * mm});
            skSolve(sketch);
        }
        {
            var Q0;
            Q0=makeQuery(id+"F24.imprint","IMPRINT",FACE,{"disambiguationData":[TD([[makeQuery(id+"F24.imprint","IMPRINT",EDGE,{"derivedFrom":sQuery(id+"F24.wireOp",EDGE,"E132.7.4")}),-1.0]])]});
            var Q1;
            Q1=makeQuery(id+"F24.imprint","IMPRINT",FACE,{"disambiguationData":[TD([[makeQuery(id+"F24.imprint","IMPRINT",EDGE,{"derivedFrom":sQuery(id+"F24.wireOp",EDGE,"E128.1")}),-1.0]])]});
            var Q2;
            Q2=makeQuery(id+"F24.imprint","IMPRINT",FACE,{"disambiguationData":[TD([[makeQuery(id+"F24.imprint","IMPRINT",EDGE,{"derivedFrom":sQuery(id+"F24.wireOp",EDGE,"E132.6.4")}),-1.0]])]});
            var Q3;
            Q3=makeQuery(id+"F24.imprint","IMPRINT",FACE,{"disambiguationData":[TD([[makeQuery(id+"F24.imprint","IMPRINT",EDGE,{"derivedFrom":sQuery(id+"F24.wireOp",EDGE,"E132.5.4")}),-1.0]])]});
            var Q4;
            Q4=makeQuery(id+"F24.imprint","IMPRINT",FACE,{"disambiguationData":[TD([[makeQuery(id+"F24.imprint","IMPRINT",EDGE,{"derivedFrom":sQuery(id+"F24.wireOp",EDGE,"E132.4.4")}),-1.0]])]});
            var Q5;
            Q5=makeQuery(id+"F24.imprint","IMPRINT",FACE,{"disambiguationData":[TD([[makeQuery(id+"F24.imprint","IMPRINT",EDGE,{"derivedFrom":sQuery(id+"F24.wireOp",EDGE,"E132.3.4")}),-1.0]])]});
            var Q6;
            Q6=makeQuery(id+"F24.imprint","IMPRINT",FACE,{"disambiguationData":[TD([[makeQuery(id+"F24.imprint","IMPRINT",EDGE,{"derivedFrom":sQuery(id+"F24.wireOp",EDGE,"E132.2.4")}),-1.0]])]});
            var Q7;
            Q7=makeQuery(id+"F24.imprint","IMPRINT",FACE,{"disambiguationData":[TD([[makeQuery(id+"F24.imprint","IMPRINT",EDGE,{"derivedFrom":sQuery(id+"F24.wireOp",EDGE,"E132.1.4")}),-1.0]])]});
            extrude(context, id + "F25", {"entities" : qUnion([Q0, Q1, Q2, Q3, Q4, Q5, Q6, Q7]), "operationType" : NewBodyOperationType.REMOVE, "oppositeDirection" : true, "depth" : (3 / 32 + getVariable(context, 'SHRINKAGE') + getVariable(context, 'CLOSE_FIT')) * mm, "offsetDistance" : 25.4 * mm});
        }
        {
            var Q0;
            Q0=qCreatedBy(makeId("Top.planeOp"),FACE);
            cPlane(context, id + "F26", {"entities" : qUnion([Q0]), "cplaneType" : CPlaneType.OFFSET, "offset" : 11.43 * mm, "oppositeDirection" : true, "width" : 152.4 * mm, "height" : 152.4 * mm});
        }
        {
            var Q0;
            Q0=qCreatedBy(id+"F26.planeOp",FACE);
            var sketch = newSketch(context, id + "F27", { "sketchPlane" : qUnion([Q0])});
            skLineSegment(sketch, "E133", {"start": v(0, 0) * mm, "end": v(0, -23.18) * mm, "construction": true});
            skLineSegment(sketch, "E134", {"start": v(0, 0) * mm, "end": v(19.45, -19.45) * mm, "construction": true});
            skCircle(sketch, "E135.cCircle", {"center": v(7.3, -7.3) * mm, "radius": 3.37 * mm, "construction": true});
            skLineSegment(sketch, "E135.0", {"start": v(8.32, -11.06) * mm, "end": v(4.56, -10.06) * mm});
            skLineSegment(sketch, "E135.1", {"start": v(4.56, -10.06) * mm, "end": v(3.56, -6.3) * mm});
            skLineSegment(sketch, "E135.2", {"start": v(3.56, -6.3) * mm, "end": v(6.3, -3.56) * mm});
            skLineSegment(sketch, "E135.3", {"start": v(6.3, -3.56) * mm, "end": v(10.06, -4.56) * mm});
            skLineSegment(sketch, "E135.4", {"start": v(10.06, -4.56) * mm, "end": v(11.06, -8.32) * mm});
            skLineSegment(sketch, "E135.5", {"start": v(11.06, -8.32) * mm, "end": v(8.32, -11.06) * mm});
            skPoint(sketch, "E135.0.midPoint", {"position": v(6.44, -10.56) * mm});
            skLineSegment(sketch, "E136", {"start": v(4.56, -10.06) * mm, "end": v(0.98, -6.48) * mm});
            skLineSegment(sketch, "E137", {"start": v(10.06, -4.56) * mm, "end": v(6.48, -0.98) * mm});
            skLineSegment(sketch, "E138", {"start": v(0.98, -6.48) * mm, "end": v(6.48, -0.98) * mm});
            skCircle(sketch, "E139.1.0", {"center": v(7.54, 7.37) * mm, "radius": 3.37 * mm, "construction": true});
            skLineSegment(sketch, "E139.1.1", {"start": v(11.3, 8.38) * mm, "end": v(10.3, 4.62) * mm});
            skLineSegment(sketch, "E139.1.2", {"start": v(10.3, 4.62) * mm, "end": v(6.54, 3.62) * mm});
            skLineSegment(sketch, "E139.1.3", {"start": v(6.54, 3.62) * mm, "end": v(3.79, 6.37) * mm});
            skLineSegment(sketch, "E139.1.4", {"start": v(4.8, 10.12) * mm, "end": v(1.21, 6.54) * mm});
            skPoint(sketch, "E139.1.5", {"position": v(10.8, 6.5) * mm});
            skLineSegment(sketch, "E139.1.6", {"start": v(10.3, 4.62) * mm, "end": v(6.71, 1.04) * mm});
            skLineSegment(sketch, "E139.1.7", {"start": v(4.8, 10.12) * mm, "end": v(8.55, 11.13) * mm});
            skLineSegment(sketch, "E139.1.8", {"start": v(6.71, 1.04) * mm, "end": v(1.21, 6.54) * mm});
            skLineSegment(sketch, "E139.1.9", {"start": v(3.79, 6.37) * mm, "end": v(4.8, 10.12) * mm});
            skLineSegment(sketch, "E139.1.10", {"start": v(8.55, 11.13) * mm, "end": v(11.3, 8.38) * mm});
            skCircle(sketch, "E139.2.0", {"center": v(-7.14, 7.6) * mm, "radius": 3.37 * mm, "construction": true});
            skLineSegment(sketch, "E139.2.1", {"start": v(-8.15, 11.36) * mm, "end": v(-4.4, 10.35) * mm});
            skLineSegment(sketch, "E139.2.2", {"start": v(-4.4, 10.35) * mm, "end": v(-3.39, 6.6) * mm});
            skLineSegment(sketch, "E139.2.3", {"start": v(-3.39, 6.6) * mm, "end": v(-6.13, 3.85) * mm});
            skLineSegment(sketch, "E139.2.4", {"start": v(-9.89, 4.86) * mm, "end": v(-6.3, 1.28) * mm});
            skPoint(sketch, "E139.2.5", {"position": v(-6.27, 10.86) * mm});
            skLineSegment(sketch, "E139.2.6", {"start": v(-4.4, 10.35) * mm, "end": v(-0.81, 6.77) * mm});
            skLineSegment(sketch, "E139.2.7", {"start": v(-9.89, 4.86) * mm, "end": v(-10.9, 8.61) * mm});
            skLineSegment(sketch, "E139.2.8", {"start": v(-0.81, 6.77) * mm, "end": v(-6.3, 1.28) * mm});
            skLineSegment(sketch, "E139.2.9", {"start": v(-6.13, 3.85) * mm, "end": v(-9.89, 4.86) * mm});
            skLineSegment(sketch, "E139.2.10", {"start": v(-10.9, 8.61) * mm, "end": v(-8.15, 11.36) * mm});
            skCircle(sketch, "E139.3.0", {"center": v(-7.37, -7.08) * mm, "radius": 3.37 * mm, "construction": true});
            skLineSegment(sketch, "E139.3.1", {"start": v(-11.13, -8.08) * mm, "end": v(-10.12, -4.33) * mm});
            skLineSegment(sketch, "E139.3.2", {"start": v(-10.12, -4.33) * mm, "end": v(-6.37, -3.32) * mm});
            skLineSegment(sketch, "E139.3.3", {"start": v(-6.37, -3.32) * mm, "end": v(-3.62, -6.07) * mm});
            skLineSegment(sketch, "E139.3.4", {"start": v(-4.62, -9.82) * mm, "end": v(-1.04, -6.24) * mm});
            skPoint(sketch, "E139.3.5", {"position": v(-10.62, -6.2) * mm});
            skLineSegment(sketch, "E139.3.6", {"start": v(-10.12, -4.33) * mm, "end": v(-6.54, -0.75) * mm});
            skLineSegment(sketch, "E139.3.7", {"start": v(-4.62, -9.82) * mm, "end": v(-8.38, -10.83) * mm});
            skLineSegment(sketch, "E139.3.8", {"start": v(-6.54, -0.75) * mm, "end": v(-1.04, -6.24) * mm});
            skLineSegment(sketch, "E139.3.9", {"start": v(-3.62, -6.07) * mm, "end": v(-4.62, -9.82) * mm});
            skLineSegment(sketch, "E139.3.10", {"start": v(-8.38, -10.83) * mm, "end": v(-11.13, -8.08) * mm});
            skPoint(sketch, "E139.center", {"position": v(0.09, 0.15) * mm});
            skSolve(sketch);
        }
        {
            var Q0;
            Q0=makeQuery(id+"F27.imprint","IMPRINT",FACE,{"disambiguationData":[TD([[makeQuery(id+"F27.imprint","IMPRINT",EDGE,{"derivedFrom":sQuery(id+"F27.wireOp",EDGE,"E139.3.1")}),-1.0]])]});
            var Q1;
            Q1=makeQuery(id+"F27.imprint","IMPRINT",FACE,{"disambiguationData":[TD([[makeQuery(id+"F27.imprint","IMPRINT",EDGE,{"derivedFrom":sQuery(id+"F27.wireOp",EDGE,"E139.3.2")}),1.0]])]});
            var Q2;
            Q2=makeQuery(id+"F27.imprint","IMPRINT",FACE,{"disambiguationData":[TD([[makeQuery(id+"F27.imprint","IMPRINT",EDGE,{"derivedFrom":sQuery(id+"F27.wireOp",EDGE,"E139.2.1")}),-1.0]])]});
            var Q3;
            Q3=makeQuery(id+"F27.imprint","IMPRINT",FACE,{"disambiguationData":[TD([[makeQuery(id+"F27.imprint","IMPRINT",EDGE,{"derivedFrom":sQuery(id+"F27.wireOp",EDGE,"E139.2.2")}),1.0]])]});
            var Q4;
            Q4=makeQuery(id+"F27.imprint","IMPRINT",FACE,{"disambiguationData":[TD([[makeQuery(id+"F27.imprint","IMPRINT",EDGE,{"derivedFrom":sQuery(id+"F27.wireOp",EDGE,"E139.1.2")}),1.0]])]});
            var Q5;
            Q5=makeQuery(id+"F27.imprint","IMPRINT",FACE,{"disambiguationData":[TD([[makeQuery(id+"F27.imprint","IMPRINT",EDGE,{"derivedFrom":sQuery(id+"F27.wireOp",EDGE,"E135.1")}),1.0]])]});
            var Q6;
            Q6=makeQuery(id+"F27.imprint","IMPRINT",FACE,{"disambiguationData":[TD([[makeQuery(id+"F27.imprint","IMPRINT",EDGE,{"derivedFrom":sQuery(id+"F27.wireOp",EDGE,"E135.0")}),-1.0]])]});
            var Q7;
            Q7=makeQuery(id+"F27.imprint","IMPRINT",FACE,{"disambiguationData":[TD([[makeQuery(id+"F27.imprint","IMPRINT",EDGE,{"derivedFrom":sQuery(id+"F27.wireOp",EDGE,"E139.1.1")}),-1.0]])]});
            extrude(context, id + "F28", {"entities" : qUnion([Q0, Q1, Q2, Q3, Q4, Q5, Q6, Q7]), "operationType" : NewBodyOperationType.REMOVE, "oppositeDirection" : true, "depth" : (3 / 32 + getVariable(context, 'SHRINKAGE') + getVariable(context, 'CLOSE_FIT')) * mm, "offsetDistance" : 25.4 * mm});
        }
    });
